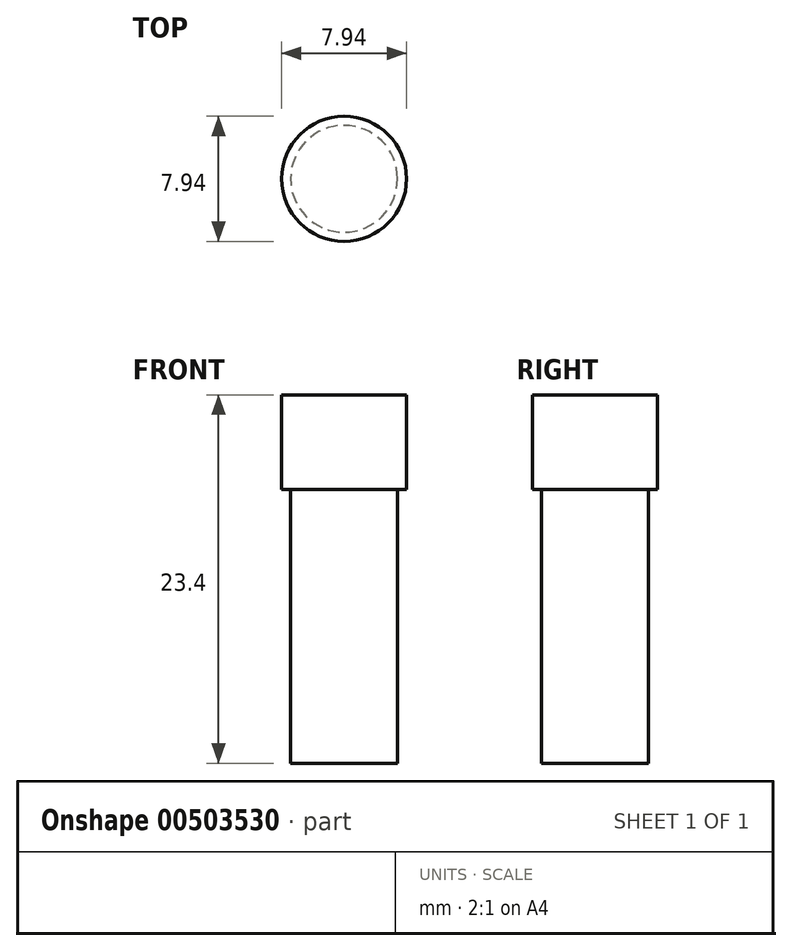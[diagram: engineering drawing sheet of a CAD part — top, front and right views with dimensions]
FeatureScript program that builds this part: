
annotation { "Feature Type Name" : "Feature", "Feature Type Description" : "" }
export const myFeature = defineFeature(function(context is Context, id is Id, definition is map)
    precondition{}
    {
        {
            var Q0;
            Q0=qCreatedBy(makeId("Top.planeOp"),FACE);
            var sketch = newSketch(context, id + "F0", { "sketchPlane" : qUnion([Q0])});
            skCircle(sketch, "E0", {"center": v(-39.6, 50.87) * mm, "radius": 3.97 * mm});
            skCircle(sketch, "E1", {"center": v(-39.6, 50.87) * mm, "radius": 3.1 * mm});
            skSolve(sketch);
        }
        {
            var Q0;
            Q0 = qSketchRegion(id + "F0", true);
            var Q1;
            Q1=makeQuery(id+"F0.imprint","IMPRINT",FACE,{"disambiguationData":[TD([[makeQuery(id+"F0.imprint","IMPRINT",EDGE,{"derivedFrom":sQuery(id+"F0.wireOp",EDGE,"E1")}),1.0]])]});
            extrude(context, id + "F1", {"entities" : qUnion([Q0, Q1]), "depth" : 6 * mm});
        }
        {
            var Q0;
            Q0=makeQuery(id+"F1.opExtrude","CAP_FACE",FACE,{"disambiguationData":[OSD([sQuery(id+"F0.wireOp",EDGE,"E0"),sQuery(id+"F0.wireOp",EDGE,"E1")])],"isStart":true});
            var sketch = newSketch(context, id + "F2", { "sketchPlane" : qUnion([Q0])});
            skCircle(sketch, "E2", {"center": v(-39.6, -50.87) * mm, "radius": 3.4 * mm});
            skSolve(sketch);
        }
        {
            var Q0;
            Q0 = qSketchRegion(id + "F2", true);
            var Q1;
            Q1=makeQuery(id+"F2.imprint","IMPRINT",FACE,{"disambiguationData":[TD([[makeQuery(id+"F2.imprint","IMPRINT",EDGE,{"derivedFrom":sQuery(id+"F2.wireOp",EDGE,"Ww8Ti6tY-IG9a-x12v-wMIw-u2TN2AwnsFea")}),1.0]])]});
            extrude(context, id + "F3", {"entities" : qUnion([Q0, Q1]), "operationType" : NewBodyOperationType.ADD, "depth" : 17.4 * mm});
        }
    });
